# Revit family: Graypants_Barro6_Pendant_R21_0925
name_source: partatom
category: Lighting Fixtures
units: mm (PartAtom-declared; Revit-internal decimal feet)

## family parameters
Cut with Voids When Loaded = No
Host = Face
Light Source = Yes
Part Type = Normal
Room Calculation Point = No
Round Connector Dimension = Use Diameter
Shared = No

## types (1)
- Graypants_Barro6_Pendant (6" diameter)
    Color Filter = 16777215
    Default Elevation = 4' - 0"
    Dimming Lamp Color Temperature Shift = <None>
    Emit Shape Visible in Rendering = No
    Emit from Circle Diameter = 2' - 0"
    Graypants_Apparent_Load = E26 - Max 15W LED | 
Optional Integrated LED - 12W
    Graypants_Barro6_Shade_Visible = Yes
    Graypants_Canopy_Material_Finish = _Graypants_Black_Finish
    Graypants_Canopy_Visible = Yes
    Graypants_Cord/Canopy_Finish_Options = Black
    Graypants_Cord_Material_Finish = _Graypants_Black_Finish
    Graypants_Cord_Visible = Yes
    Graypants_Description = In partnership with Caterina Moretti of Peca design studio, Barro is a handmade pendant 
with a ceramic base and glass shade; a beautiful marriage of natural materials
that quite literally starts from the earth of Oaxaca.
    Graypants_Dimming = E26 - Depending on lamp
 | Optional Integrated LED - 0-10v or Triac/ELV
    Graypants_Initial_Color_Temperature = E26 - 2700K Recommended | 
Optional Integrated LED - 2700K
    Graypants_Initial_Intensity = E26 - 800 Lumen Lamp Recommended
 | Optional Integrated LED - 926 Lumens
    Graypants_Manufacturer = Graypants
    Graypants_Model = Barro6
    Graypants_SKU = Natural/Clear - GP2700-NC | 
Charcoal/Smoke - GP2701-CS
    Graypants_Shade_Finish_Options = Clay - Natural / Glass - Clear | 
Clay - Charcoal / Glass - Smoke
    Graypants_Spec_Sheet = https://www.dropbox.com
    Graypants_URL = www.graypants.com
    Graypants_Voltage = E26 - 120V | 
Optional Integrated LED - 120-277V
    Light Source Symbol Size = 0' - 6 9/16"

## geometry (parser evidence)
native form markers: Sweep x7
no freeform markers — native parametric forms only
